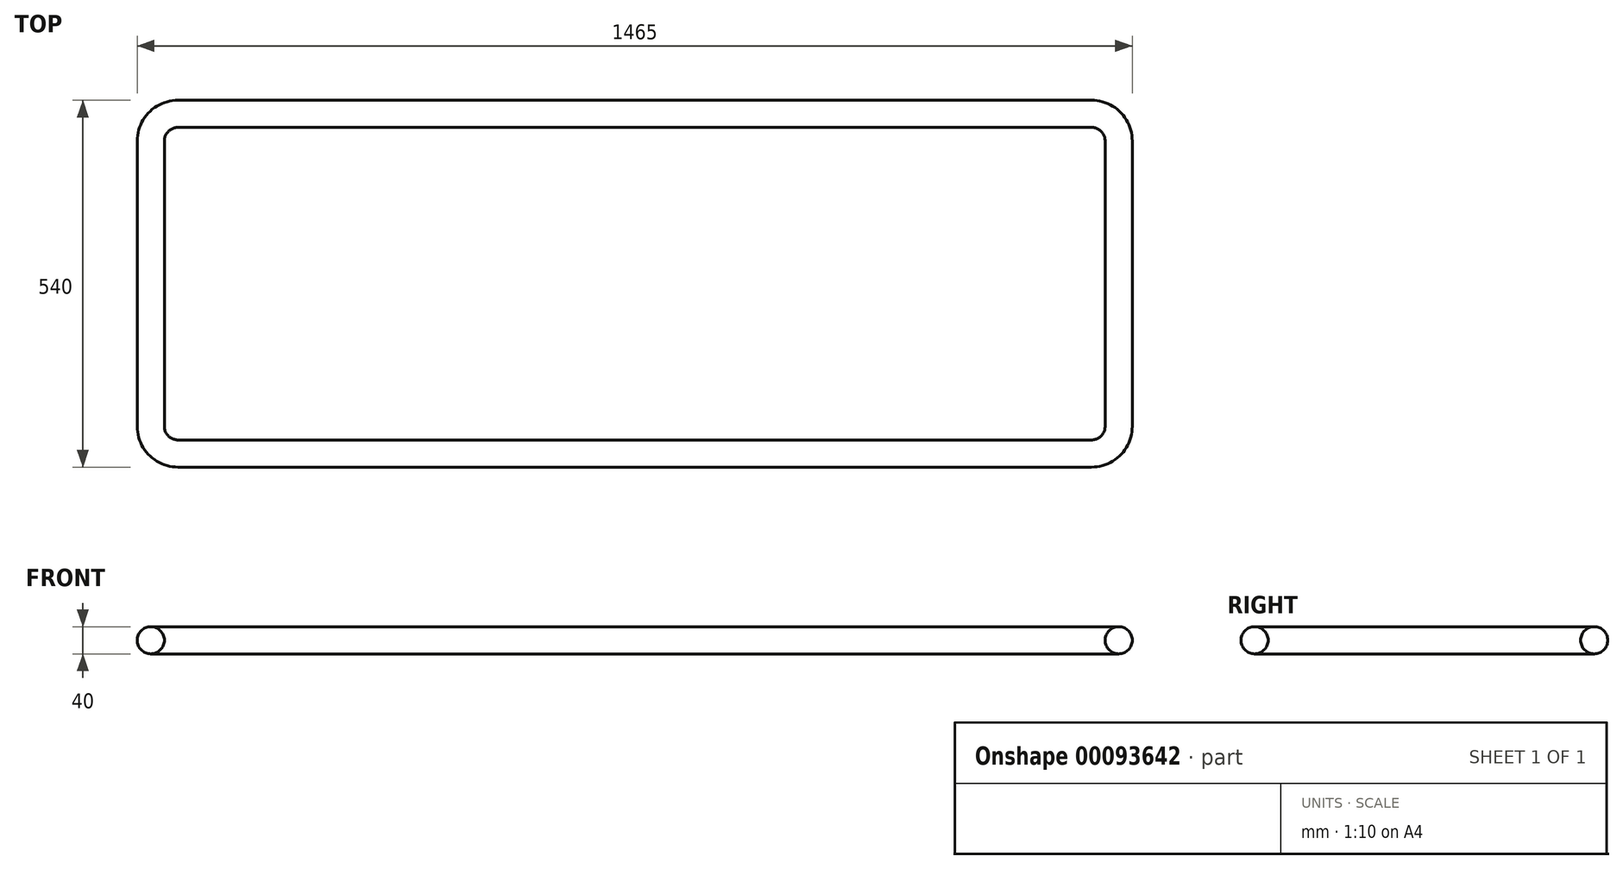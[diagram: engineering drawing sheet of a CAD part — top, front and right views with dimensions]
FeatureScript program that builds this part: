
annotation { "Feature Type Name" : "Feature", "Feature Type Description" : "" }
export const myFeature = defineFeature(function(context is Context, id is Id, definition is map)
    precondition{}
    {
        {
            var Q0;
            Q0=qCreatedBy(makeId("Top.planeOp"),FACE);
            var sketch = newSketch(context, id + "F0", { "sketchPlane" : qUnion([Q0])});
            skLineSegment(sketch, "E0.bottom", {"start": v(-672.5, -250) * mm, "end": v(672.5, -250) * mm});
            skLineSegment(sketch, "E0.top", {"start": v(-672.5, 250) * mm, "end": v(672.5, 250) * mm});
            skLineSegment(sketch, "E0.left", {"start": v(-712.5, -210) * mm, "end": v(-712.5, 210) * mm});
            skLineSegment(sketch, "E0.right", {"start": v(712.5, -210) * mm, "end": v(712.5, 210) * mm});
            skPoint(sketch, "E0.middle", {"position": v(0, 0) * mm});
            skPoint(sketch, "E1.visualSharp", {"position": v(-712.5, 250) * mm});
            skArc(sketch, "E1.filletArc", {"start": v(-672.5, 250) * mm, "mid": v(-700.78, 238.28) * mm, "end": v(-712.5, 210) * mm});
            skPoint(sketch, "E2.visualSharp", {"position": v(712.5, 250) * mm});
            skArc(sketch, "E2.filletArc", {"start": v(712.5, 210) * mm, "mid": v(700.78, 238.28) * mm, "end": v(672.5, 250) * mm});
            skPoint(sketch, "E3.visualSharp", {"position": v(712.5, -250) * mm});
            skArc(sketch, "E3.filletArc", {"start": v(672.5, -250) * mm, "mid": v(700.78, -238.28) * mm, "end": v(712.5, -210) * mm});
            skPoint(sketch, "E4.visualSharp", {"position": v(-712.5, -250) * mm});
            skArc(sketch, "E4.filletArc", {"start": v(-712.5, -210) * mm, "mid": v(-700.78, -238.28) * mm, "end": v(-672.5, -250) * mm});
            skSolve(sketch);
        }
        {
            var Q0;
            Q0=qCreatedBy(makeId("Right.planeOp"),FACE);
            cPlane(context, id + "F1", {"entities" : qUnion([Q0]), "cplaneType" : CPlaneType.OFFSET, "offset" : 672.5 * mm, "width" : 150 * mm, "height" : 150 * mm});
        }
        {
            var Q0;
            Q0=qCreatedBy(id+"F1.planeOp",FACE);
            var sketch = newSketch(context, id + "F2", { "sketchPlane" : qUnion([Q0])});
            skCircle(sketch, "E5", {"center": v(250, 0) * mm, "radius": 20 * mm});
            skSolve(sketch);
        }
        {
            var Q0;
            Q0=makeQuery(id+"F2.imprint","IMPRINT",FACE,{"disambiguationData":[TD([[makeQuery(id+"F2.imprint","IMPRINT",EDGE,{"derivedFrom":sQuery(id+"F2.wireOp",EDGE,"E5")}),1.0]])]});
            var Q1;
            Q1=sQuery(id+"F0.wireOp",EDGE,"E0.top");
            var Q2;
            Q2=sQuery(id+"F0.wireOp",EDGE,"E0.left");
            var Q3;
            Q3=sQuery(id+"F0.wireOp",EDGE,"E1.filletArc");
            var Q4;
            Q4=sQuery(id+"F0.wireOp",EDGE,"E4.filletArc");
            var Q5;
            Q5=sQuery(id+"F0.wireOp",EDGE,"E0.bottom");
            var Q6;
            Q6=sQuery(id+"F0.wireOp",EDGE,"E3.filletArc");
            var Q7;
            Q7=sQuery(id+"F0.wireOp",EDGE,"E0.right");
            var Q8;
            Q8=sQuery(id+"F0.wireOp",EDGE,"E2.filletArc");
            sweep(context, id + "F3", {"profiles" : qUnion([Q0]), "path" : qUnion([Q1, Q2, Q3, Q4, Q5, Q6, Q7, Q8])});
        }
    });
